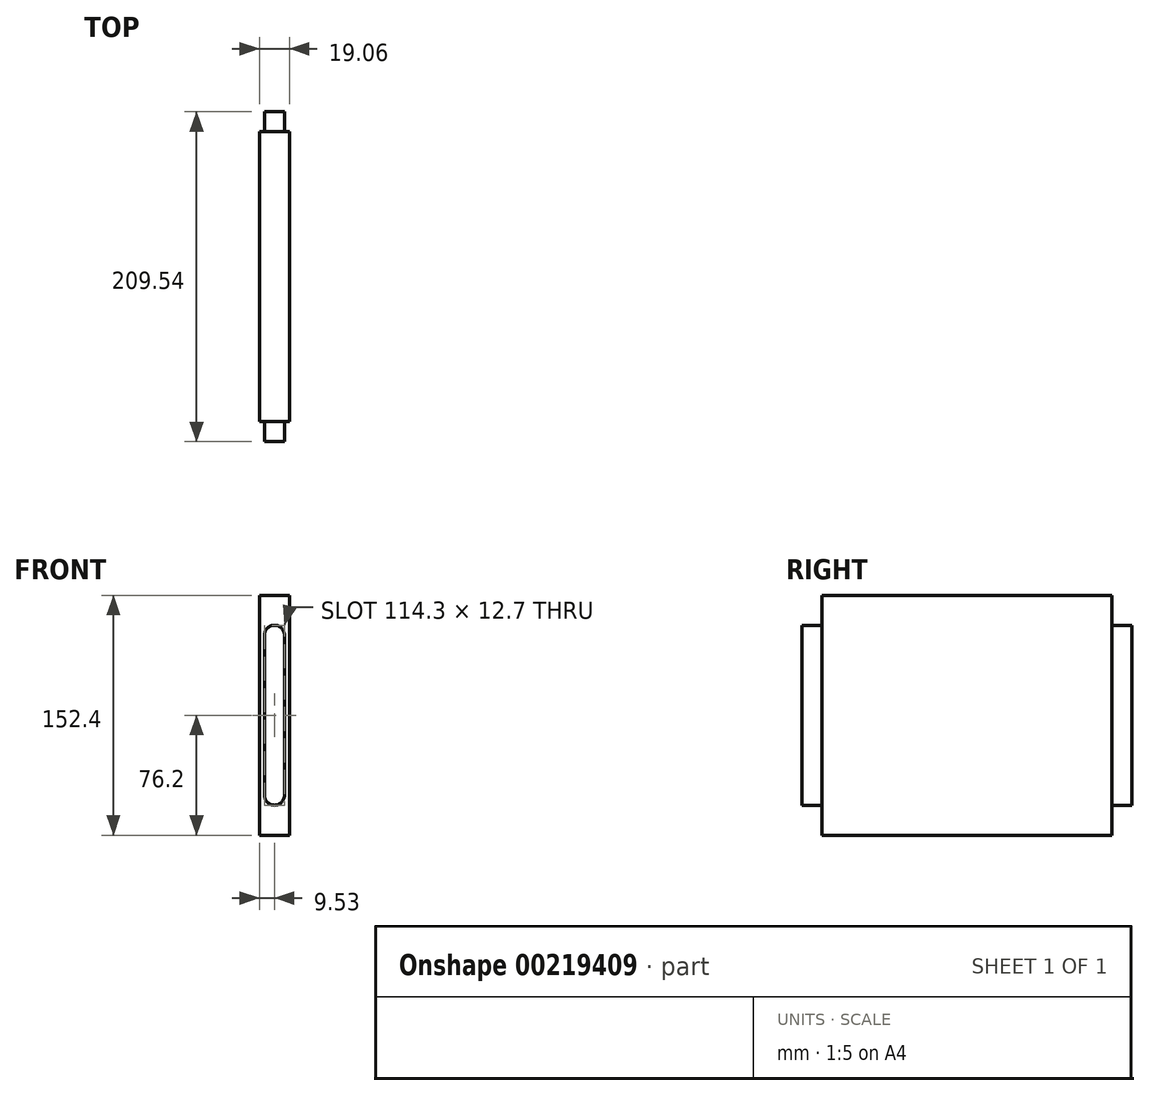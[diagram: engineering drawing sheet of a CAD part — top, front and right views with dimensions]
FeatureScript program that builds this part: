
annotation { "Feature Type Name" : "Feature", "Feature Type Description" : "" }
export const myFeature = defineFeature(function(context is Context, id is Id, definition is map)
    precondition{}
    {
        {
            var Q0;
            Q0=qCreatedBy(makeId("Top.planeOp"),FACE);
            var sketch = newSketch(context, id + "F0", { "sketchPlane" : qUnion([Q0])});
            skLineSegment(sketch, "E0.bottom", {"start": v(-9.53, -92.08) * mm, "end": v(9.52, -92.08) * mm});
            skLineSegment(sketch, "E0.top", {"start": v(-9.53, 92.07) * mm, "end": v(9.52, 92.07) * mm});
            skLineSegment(sketch, "E0.left", {"start": v(-9.53, -92.08) * mm, "end": v(-9.53, 92.07) * mm});
            skLineSegment(sketch, "E0.right", {"start": v(9.52, -92.08) * mm, "end": v(9.52, 92.07) * mm});
            skPoint(sketch, "E0.middle", {"position": v(0, 0) * mm});
            skSolve(sketch);
        }
        {
            var Q0;
            Q0 = qSketchRegion(id + "F0", true);
            extrude(context, id + "F1", {"entities" : qUnion([Q0]), "oppositeDirection" : true, "depth" : 152.4 * mm, "offsetDistance" : 25.4 * mm});
        }
        {
            var Q0;
            Q0=makeQuery(id+"F1.opExtrude","SWEPT_FACE",FACE,{"disambiguationData":[OSD([sQuery(id+"F0.wireOp",EDGE,"E0.bottom")])]});
            var sketch = newSketch(context, id + "F2", { "sketchPlane" : qUnion([Q0])});
            skLineSegment(sketch, "E1.bottom", {"start": v(-6.35, -133.35) * mm, "end": v(6.35, -133.35) * mm});
            skLineSegment(sketch, "E1.top", {"start": v(-6.35, -19.05) * mm, "end": v(6.35, -19.05) * mm});
            skLineSegment(sketch, "E1.left", {"start": v(-6.35, -133.35) * mm, "end": v(-6.35, -19.05) * mm});
            skLineSegment(sketch, "E1.right", {"start": v(6.35, -133.35) * mm, "end": v(6.35, -19.05) * mm});
            skPoint(sketch, "E1.middle", {"position": v(0, -76.2) * mm});
            skSolve(sketch);
        }
        {
            var Q0;
            Q0 = qSketchRegion(id + "F2", true);
            extrude(context, id + "F3", {"entities" : qUnion([Q0]), "operationType" : NewBodyOperationType.ADD, "depth" : 12.7 * mm, "offsetDistance" : 25.4 * mm});
        }
        {
            var Q0;
            Q0=makeQuery(id+"F1.opExtrude","SWEPT_FACE",FACE,{"disambiguationData":[OSD([sQuery(id+"F0.wireOp",EDGE,"E0.top")])]});
            var sketch = newSketch(context, id + "F4", { "sketchPlane" : qUnion([Q0])});
            skLineSegment(sketch, "E2.bottom", {"start": v(-6.35, -133.35) * mm, "end": v(6.35, -133.35) * mm});
            skLineSegment(sketch, "E2.top", {"start": v(-6.35, -19.05) * mm, "end": v(6.35, -19.05) * mm});
            skLineSegment(sketch, "E2.left", {"start": v(-6.35, -133.35) * mm, "end": v(-6.35, -19.05) * mm});
            skLineSegment(sketch, "E2.right", {"start": v(6.35, -133.35) * mm, "end": v(6.35, -19.05) * mm});
            skPoint(sketch, "E2.middle", {"position": v(0, -76.2) * mm});
            skSolve(sketch);
        }
        {
            var Q0;
            Q0 = qSketchRegion(id + "F4", true);
            extrude(context, id + "F5", {"entities" : qUnion([Q0]), "operationType" : NewBodyOperationType.ADD, "depth" : 12.7 * mm, "offsetDistance" : 25.4 * mm});
        }
        {
            var Q0;
            Q0=makeQuery(id+"F5.opExtrude","SWEPT_EDGE",EDGE,{"disambiguationData":[OSD([sQuery(id+"F4.wireOp",EDGE,"E2.top"),sQuery(id+"F4.wireOp",EDGE,"E2.left")])]});
            var Q1;
            Q1=makeQuery(id+"F5.opExtrude","SWEPT_EDGE",EDGE,{"disambiguationData":[OSD([sQuery(id+"F4.wireOp",EDGE,"E2.top"),sQuery(id+"F4.wireOp",EDGE,"E2.right")])]});
            var Q2;
            Q2=makeQuery(id+"F5.opExtrude","SWEPT_EDGE",EDGE,{"disambiguationData":[OSD([sQuery(id+"F4.wireOp",EDGE,"E2.bottom"),sQuery(id+"F4.wireOp",EDGE,"E2.right")])]});
            var Q3;
            Q3=makeQuery(id+"F5.opExtrude","SWEPT_EDGE",EDGE,{"disambiguationData":[OSD([sQuery(id+"F4.wireOp",EDGE,"E2.bottom"),sQuery(id+"F4.wireOp",EDGE,"E2.left")])]});
            var Q4;
            Q4=makeQuery(id+"F3.opExtrude","SWEPT_EDGE",EDGE,{"disambiguationData":[OSD([sQuery(id+"F2.wireOp",EDGE,"E1.top"),sQuery(id+"F2.wireOp",EDGE,"E1.left")])]});
            var Q5;
            Q5=makeQuery(id+"F3.opExtrude","SWEPT_EDGE",EDGE,{"disambiguationData":[OSD([sQuery(id+"F2.wireOp",EDGE,"E1.top"),sQuery(id+"F2.wireOp",EDGE,"E1.right")])]});
            var Q6;
            Q6=makeQuery(id+"F3.opExtrude","SWEPT_EDGE",EDGE,{"disambiguationData":[OSD([sQuery(id+"F2.wireOp",EDGE,"E1.bottom"),sQuery(id+"F2.wireOp",EDGE,"E1.left")])]});
            var Q7;
            Q7=makeQuery(id+"F3.opExtrude","SWEPT_EDGE",EDGE,{"disambiguationData":[OSD([sQuery(id+"F2.wireOp",EDGE,"E1.bottom"),sQuery(id+"F2.wireOp",EDGE,"E1.right")])]});
            fillet(context, id + "F6", {"entities" : qUnion([Q0, Q1, Q2, Q3, Q4, Q5, Q6, Q7]), "radius" : 6.35 * mm, "tangentPropagation" : true, "allowEdgeOverflow" : false});
        }
    });
